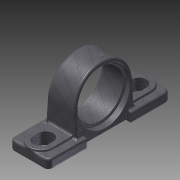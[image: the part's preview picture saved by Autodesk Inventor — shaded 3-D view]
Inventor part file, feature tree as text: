
AUTODESK INVENTOR PART (.ipt)
format: ipt  version: 2012 (Build 160160000, 160)  size: 676,864 bytes
history: native  units: mm
features: fillet x9, sketch x7, extrude x6, revolve x2, mirror x1, plane x1, projected_geometry x1
ambient origin geometry x8: Origin, YZ Plane, XZ Plane, XY Plane, X Axis, Y Axis, Z Axis, Center Point
bodies: Solid1 (feature_tree)
feature tree (27):
  sketch  "Sketch1"  dims[d0=60.0mm d2=3.0mm]
  revolve  "Revolution1"  [1 undecoded]
  sketch  "Sketch2"  dims[d3=4.0mm d4=3.0mm]
  revolve  "Revolution2"  [1 undecoded]
  extrude  "Extrusion2"  Depth=3.0mm
  extrude  "Extrusion3"  Depth=12.5mm
  extrude  "Extrusion4"  Depth=2.0mm
  extrude  "Extrusion5"  Depth=33.0mm TaperAngle=0.0deg
  extrude  "Extrusion6"  Depth=40.0mm
  mirror  "Mirror1"
  fillet  "Fillet1"  Radius=3.0mm
  fillet  "Fillet2"  Radius=40.0mm
  fillet  "Fillet3"  Radius=40.0mm
  fillet  "Fillet4"  Radius=12.5mm
  fillet  "Fillet5"  Radius=12.5mm
  fillet  "Fillet6"  Radius=12.5mm
  fillet  "Fillet7"  Radius=5.0mm
  fillet  "Fillet8"  Radius=5.0mm
  fillet  "Fillet9"  Radius=5.0mm
  plane  "Work Plane1"
  extrude  "Extrusion7"  Depth=2.0mm TaperAngle=0.0deg
  sketch  "Sketch3"  dims[d5=6.0mm d6=3.0mm]
  sketch  "Sketch4"  dims[d7=90.0deg d8=12.5mm]
  sketch  "Sketch5"  dims[d9=12.5mm d12=2.0mm]
  sketch  "Sketch6"  dims[d13=90.0deg d14=33.0mm d15=0.0mm]
  sketch  "Sketch7"  dims[d16=33.0mm d17=0.0mm d18=40.0mm d20=3.0mm d22=40.0mm d23=40.0mm d24=0.0mm d25=12.5mm d26=12.5mm d27=12.5mm d28=5.0mm d29=5.0mm d30=5.0mm d31=2.0mm d32=0.0mm d35=12.5mm d37=5.0mm d38=5.0mm d39=2.0mm d40=0.0mm d41=5.0mm d42=2.0mm d43=0.8mm d44=2.0mm d45=0.5mm d46=2.0mm d47=0.5mm d48=0.5mm d49=2.0mm d50=7.0mm d51=5.0mm d52=0.0mm]
  projected_geometry  "Projected Loop1"
note: 2 required parameter values undecoded (feature->parameter linkage not recoverable at this tier; creation-order binding heuristic only, values carry confidence <= 0.55)
